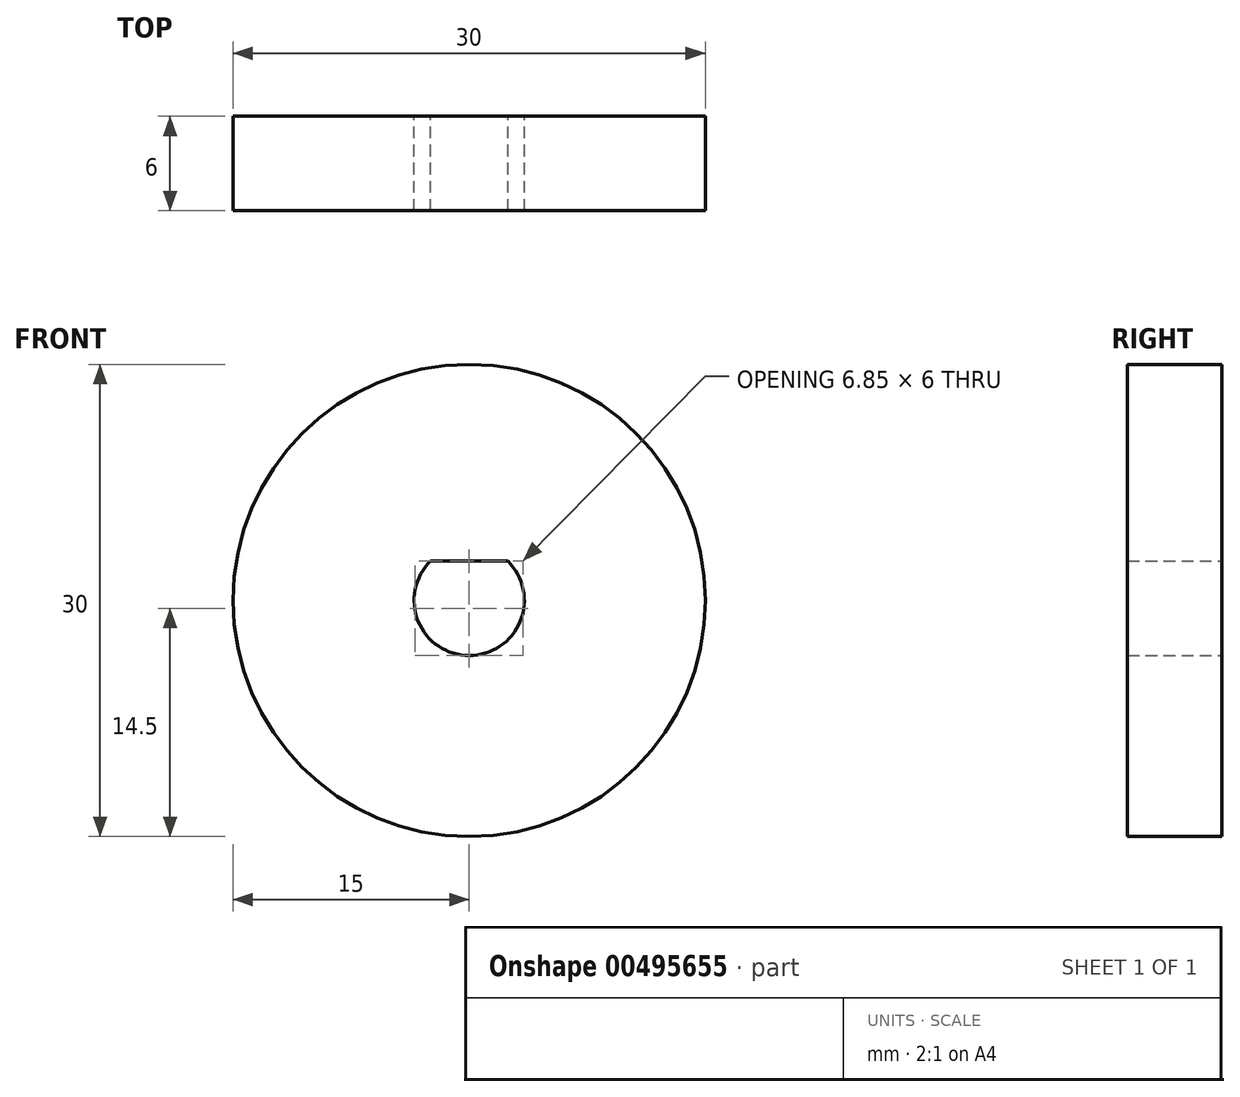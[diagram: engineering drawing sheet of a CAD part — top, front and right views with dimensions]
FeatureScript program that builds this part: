
annotation { "Feature Type Name" : "Feature", "Feature Type Description" : "" }
export const myFeature = defineFeature(function(context is Context, id is Id, definition is map)
    precondition{}
    {
        {
            var Q0;
            Q0=qCreatedBy(makeId("Front.planeOp"),FACE);
            var sketch = newSketch(context, id + "F0", { "sketchPlane" : qUnion([Q0])});
            skCircle(sketch, "E0", {"center": v(0, 0) * mm, "radius": 15 * mm});
            skArc(sketch, "E1", {"start": v(-2.45, 2.5) * mm, "mid": v(0, -3.5) * mm, "end": v(2.45, 2.5) * mm});
            skLineSegment(sketch, "E2", {"start": v(-2.45, 2.5) * mm, "end": v(2.45, 2.5) * mm});
            skPoint(sketch, "E3.start.orphan", {"position": v(3.5, 0) * mm});
            skPoint(sketch, "E4.start.orphan", {"position": v(-3.5, 0) * mm});
            skLineSegment(sketch, "E5", {"start": v(0, 2.5) * mm, "end": v(0, -3.5) * mm});
            skSolve(sketch);
        }
        {
            var Q0;
            Q0 = qSketchRegion(id + "F0", true);
            extrude(context, id + "F1", {"entities" : qUnion([Q0]), "depth" : 6 * mm});
        }
    });
